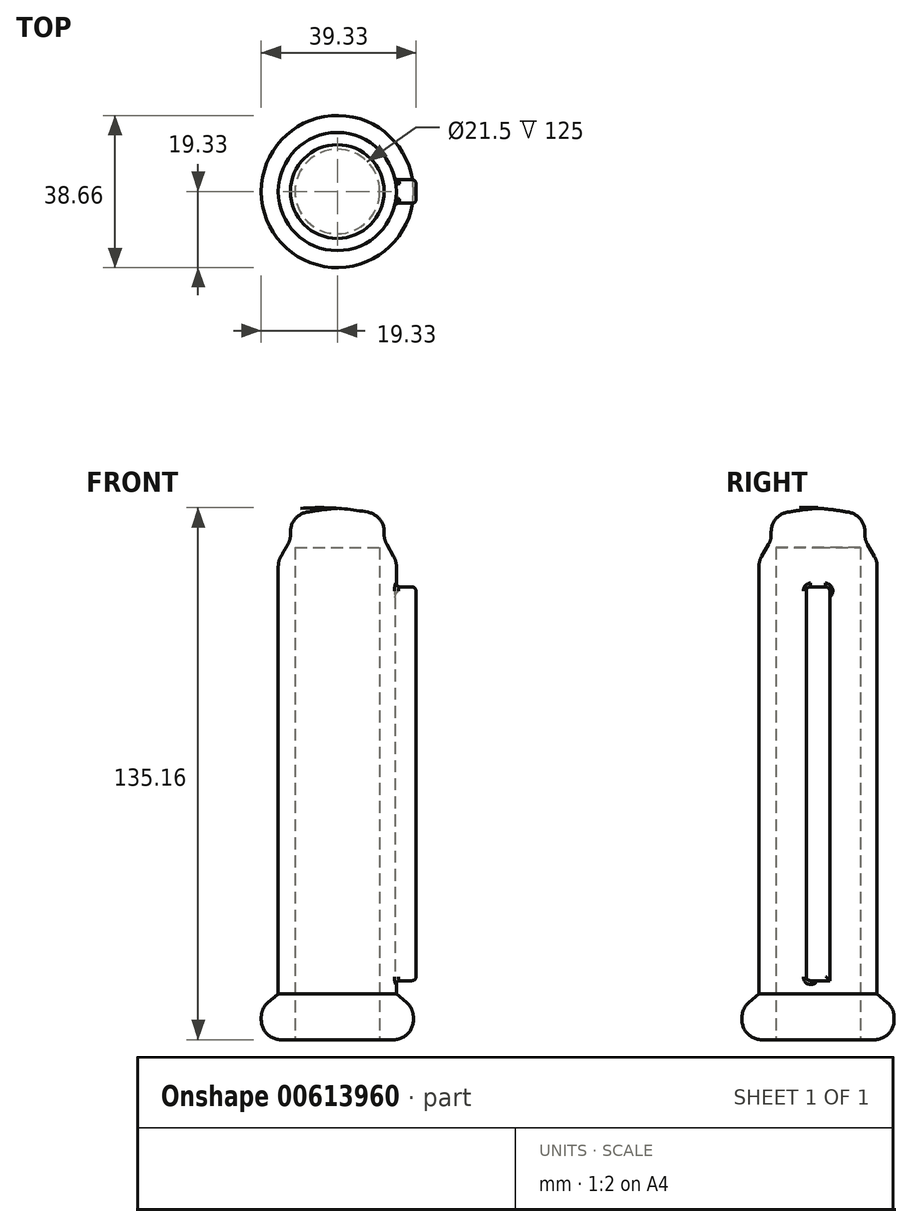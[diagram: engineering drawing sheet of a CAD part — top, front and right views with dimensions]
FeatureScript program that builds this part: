
annotation { "Feature Type Name" : "Feature", "Feature Type Description" : "" }
export const myFeature = defineFeature(function(context is Context, id is Id, definition is map)
    precondition{}
    {
        {
            var Q0;
            Q0=qCreatedBy(makeId("Front.planeOp"),FACE);
            var sketch = newSketch(context, id + "F0", { "sketchPlane" : qUnion([Q0])});
            skLineSegment(sketch, "E0", {"start": v(10.75, 0) * mm, "end": v(10.75, 125) * mm});
            skLineSegment(sketch, "E1", {"start": v(10.75, 125) * mm, "end": v(0, 125) * mm});
            skLineSegment(sketch, "E2", {"start": v(0, 125) * mm, "end": v(0, 135) * mm});
            skArc(sketch, "E3", {"start": v(11.9, 133.1) * mm, "mid": v(6, 134.32) * mm, "end": v(0, 135) * mm});
            skLineSegment(sketch, "E4", {"start": v(11.9, 133.1) * mm, "end": v(11.9, 127) * mm});
            skLineSegment(sketch, "E5", {"start": v(11.9, 127) * mm, "end": v(15, 121.63) * mm});
            skLineSegment(sketch, "E6", {"start": v(15, 121.63) * mm, "end": v(15, 11.63) * mm});
            skLineSegment(sketch, "E7", {"start": v(15, 11.63) * mm, "end": v(19.33, 8) * mm});
            skLineSegment(sketch, "E8", {"start": v(19.33, 8) * mm, "end": v(19.33, 0) * mm});
            skLineSegment(sketch, "E9", {"start": v(19.33, 0) * mm, "end": v(10.75, 0) * mm});
            skLineSegment(sketch, "E10", {"start": v(0, 0) * mm, "end": v(0, 142.55) * mm, "construction": true});
            skSolve(sketch);
        }
        {
            var Q0;
            Q0=makeQuery(id+"F0.imprint","IMPRINT",FACE,{"disambiguationData":[TD([[makeQuery(id+"F0.imprint","IMPRINT",EDGE,{"derivedFrom":sQuery(id+"F0.wireOp",EDGE,"E0")}),-1.0]])]});
            var Q1;
            Q1=sQuery(id+"F0.wireOp",EDGE,"E10");
            revolve(context, id + "F1", {"surfaceOperationType" : NewSurfaceOperationType.NEW, "entities" : qUnion([Q0]), "axis" : qUnion([Q1]), "revolveType" : RevolveType.FULL});
        }
        {
            var Q0;
            Q0=makeQuery(id+"F1.opRevolve","SWEPT_EDGE",EDGE,{"disambiguationData":[OSD([sQuery(id+"F0.wireOp",EDGE,"E3"),sQuery(id+"F0.wireOp",EDGE,"E4")])]});
            var Q1;
            Q1=makeQuery(id+"F1.opRevolve","SWEPT_FACE",FACE,{"disambiguationData":[OSD([sQuery(id+"F0.wireOp",EDGE,"E5")])]});
            var Q2;
            Q2=makeQuery(id+"F1.opRevolve","SWEPT_EDGE",EDGE,{"disambiguationData":[OSD([sQuery(id+"F0.wireOp",EDGE,"E7"),sQuery(id+"F0.wireOp",EDGE,"E8")])]});
            var Q3;
            Q3=makeQuery(id+"F1.opRevolve","SWEPT_EDGE",EDGE,{"disambiguationData":[OSD([sQuery(id+"F0.wireOp",EDGE,"E8"),sQuery(id+"F0.wireOp",EDGE,"E9")])]});
            fillet(context, id + "F2", {"entities" : qUnion([Q0, Q1, Q2, Q3]), "radius" : 5 * mm, "tangentPropagation" : true, "allowEdgeOverflow" : false});
        }
        {
            var Q0;
            Q0=qCreatedBy(makeId("Right.planeOp"),FACE);
            cPlane(context, id + "F3", {"entities" : qUnion([Q0]), "cplaneType" : CPlaneType.OFFSET, "offset" : 20 * mm, "width" : 150 * mm, "height" : 150 * mm});
        }
        {
            var Q0;
            Q0=qCreatedBy(id+"F3.planeOp",FACE);
            var sketch = newSketch(context, id + "F4", { "sketchPlane" : qUnion([Q0])});
            skLineSegment(sketch, "E11.bottom", {"start": v(-3, 115) * mm, "end": v(3, 115) * mm});
            skLineSegment(sketch, "E11.top", {"start": v(-3, 15) * mm, "end": v(3, 15) * mm});
            skLineSegment(sketch, "E11.left", {"start": v(-3, 115) * mm, "end": v(-3, 15) * mm});
            skLineSegment(sketch, "E11.right", {"start": v(3, 115) * mm, "end": v(3, 15) * mm});
            skSolve(sketch);
        }
        {
            var Q0;
            Q0 = qSketchRegion(id + "F4", true);
            var Q1;
            Q1=makeQuery(id+"F1.opRevolve","SWEPT_FACE",FACE,{"disambiguationData":[OSD([sQuery(id+"F0.wireOp",EDGE,"E6")])]});
            extrude(context, id + "F5", {"entities" : qUnion([Q0]), "operationType" : NewBodyOperationType.ADD, "endBound" : BoundingType.UP_TO_SURFACE, "oppositeDirection" : true, "depth" : 25 * mm, "endBoundEntityFace" : qUnion([Q1]), "offsetDistance" : 25 * mm});
        }
        {
            var Q0;
            Q0=makeQuery(id+"F5.opExtrude","CAP_FACE",FACE,{"disambiguationData":[OSD([sQuery(id+"F4.wireOp",EDGE,"E11.bottom"),sQuery(id+"F4.wireOp",EDGE,"E11.top"),sQuery(id+"F4.wireOp",EDGE,"E11.left"),sQuery(id+"F4.wireOp",EDGE,"E11.right")])],"isStart":true});
            var Q1;
            Q1=makeQuery(id+"F5.opExtrude","SWEPT_FACE",FACE,{"disambiguationData":[OSD([sQuery(id+"F4.wireOp",EDGE,"E11.left")])]});
            var Q2;
            Q2=makeQuery(id+"F5.opExtrude","TWEAK_EDGE",EDGE,{"derivedFrom":[makeQuery(id+"F1.opRevolve","SWEPT_FACE",FACE,{"disambiguationData":[OSD([sQuery(id+"F0.wireOp",EDGE,"E6")])]}),makeQuery(id+"F4.imprint","IMPRINT",EDGE,{"derivedFrom":sQuery(id+"F4.wireOp",EDGE,"E11.right")})]});
            var Q3;
            Q3=makeQuery(id+"F5.opExtrude","SWEPT_FACE",FACE,{"disambiguationData":[OSD([sQuery(id+"F4.wireOp",EDGE,"E11.bottom")])]});
            fillet(context, id + "F6", {"entities" : qUnion([Q0, Q1, Q2, Q3]), "radius" : 1 * mm, "tangentPropagation" : true, "allowEdgeOverflow" : false});
        }
    });
